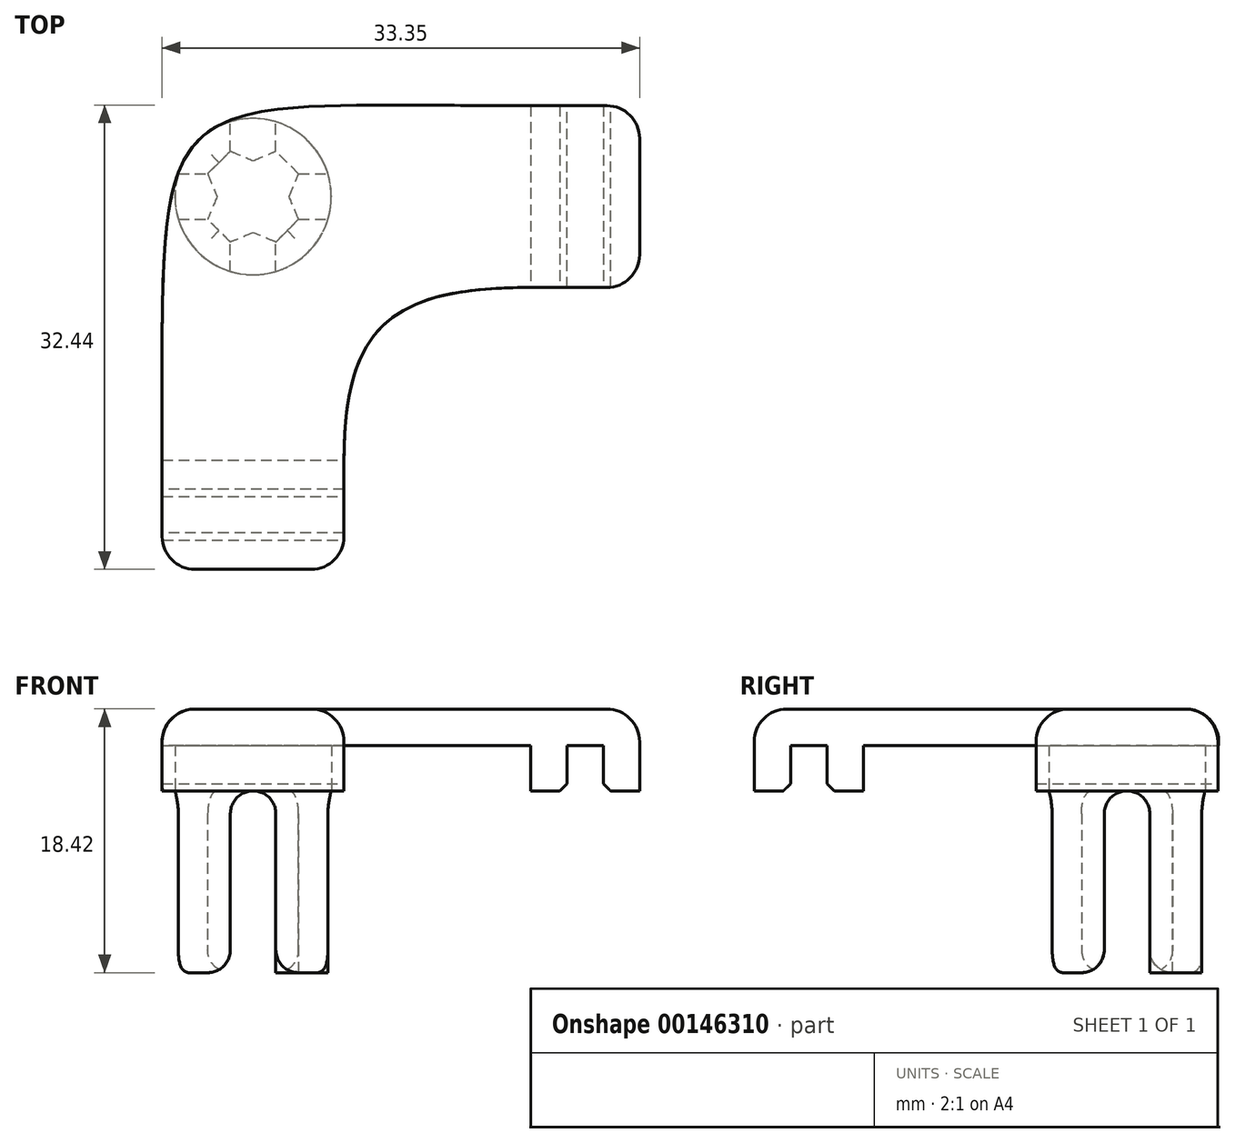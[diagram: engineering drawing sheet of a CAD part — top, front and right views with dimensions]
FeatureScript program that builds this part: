
annotation { "Feature Type Name" : "Feature", "Feature Type Description" : "" }
export const myFeature = defineFeature(function(context is Context, id is Id, definition is map)
    precondition{}
    {
        {
            var Q0;
            Q0=qCreatedBy(makeId("Top.planeOp"),FACE);
            var sketch = newSketch(context, id + "F0", { "sketchPlane" : qUnion([Q0])});
            skCircle(sketch, "E0", {"center": v(0, 0) * mm, "radius": 5.46 * mm});
            skLineSegment(sketch, "E1.bottom", {"start": v(6.35, -26.04) * mm, "end": v(-6.35, -26.04) * mm});
            skLineSegment(sketch, "E1.top", {"start": v(6.35, -18.41) * mm, "end": v(-6.35, -18.41) * mm});
            skLineSegment(sketch, "E1.left", {"start": v(6.35, -26.04) * mm, "end": v(6.35, -18.42) * mm});
            skLineSegment(sketch, "E1.right", {"start": v(-6.35, -26.04) * mm, "end": v(-6.35, -18.41) * mm});
            skPoint(sketch, "E1.middle", {"position": v(0, -22.23) * mm});
            skLineSegment(sketch, "E2.bottom", {"start": v(26.99, -6.35) * mm, "end": v(19.37, -6.35) * mm});
            skLineSegment(sketch, "E2.top", {"start": v(26.99, 6.35) * mm, "end": v(19.37, 6.35) * mm});
            skLineSegment(sketch, "E2.left", {"start": v(26.99, -6.35) * mm, "end": v(26.99, 6.35) * mm});
            skLineSegment(sketch, "E2.right", {"start": v(19.37, -6.35) * mm, "end": v(19.37, 6.35) * mm});
            skPoint(sketch, "E2.middle", {"position": v(23.18, 0) * mm});
            skSolve(sketch);
        }
        {
            var Q0;
            Q0 = qSketchRegion(id + "F0", true);
            extrude(context, id + "F1", {"entities" : qUnion([Q0]), "depth" : 15.88 * mm});
        }
        {
            var Q0;
            Q0=makeQuery(id+"F1.opExtrude","CAP_FACE",FACE,{"disambiguationData":[OSD([sQuery(id+"F0.wireOp",EDGE,"E0")])],"isStart":false});
            var sketch = newSketch(context, id + "F2", { "sketchPlane" : qUnion([Q0])});
            skLineSegment(sketch, "E3.0.0", {"start": v(-6.35, -26.04) * mm, "end": v(6.35, -26.04) * mm});
            skLineSegment(sketch, "E3.0.1", {"start": v(6.35, -26.04) * mm, "end": v(6.35, -18.42) * mm});
            skLineSegment(sketch, "E3.0.2", {"start": v(6.35, -18.41) * mm, "end": v(-6.35, -18.41) * mm});
            skLineSegment(sketch, "E3.0.3", {"start": v(-6.35, -18.41) * mm, "end": v(-6.35, -26.04) * mm});
            skLineSegment(sketch, "E4.0.0", {"start": v(19.37, -6.35) * mm, "end": v(26.99, -6.35) * mm});
            skLineSegment(sketch, "E4.0.1", {"start": v(26.99, -6.35) * mm, "end": v(26.99, 6.35) * mm});
            skLineSegment(sketch, "E4.0.2", {"start": v(26.99, 6.35) * mm, "end": v(19.37, 6.35) * mm});
            skLineSegment(sketch, "E4.0.3", {"start": v(19.37, 6.35) * mm, "end": v(19.37, -6.35) * mm});
            skCircle(sketch, "E5.0.0", {"center": v(0, 0) * mm, "radius": 5.46 * mm});
            skFitSpline(sketch, "E6", {"points": [v(-6.35, -18.41) * mm, v(19.37, 6.35) * mm], "startDerivative": vector(0, 81.2) * mm, "endDerivative": vector(81.2, 0) * mm});
            skLineSegment(sketch, "E7", {"start": v(-6.35, -18.41) * mm, "end": v(-6.35, 8.65) * mm, "construction": true});
            skLineSegment(sketch, "E8", {"start": v(-7.7, 6.35) * mm, "end": v(19.37, 6.35) * mm, "construction": true});
            skFitSpline(sketch, "E9", {"points": [v(6.35, -18.42) * mm, v(19.37, -6.35) * mm], "startDerivative": vector(0, 28.58) * mm, "endDerivative": vector(28.57, 0) * mm});
            skSolve(sketch);
        }
        {
            var Q0;
            Q0 = qSketchRegion(id + "F2", true);
            extrude(context, id + "F3", {"entities" : qUnion([Q0]), "operationType" : NewBodyOperationType.ADD, "depth" : 2.54 * mm});
        }
        {
            var Q0;
            Q0=makeQuery(id+"F1.opExtrude","CAP_EDGE",EDGE,{"disambiguationData":[OSD([sQuery(id+"F0.wireOp",EDGE,"E0")])],"isStart":false});
            var Q1;
            Q1=makeQuery(id+"F1.opExtrude","CAP_EDGE",EDGE,{"disambiguationData":[OSD([sQuery(id+"F0.wireOp",EDGE,"E1.top")])],"isStart":false});
            var Q2;
            Q2=makeQuery(id+"F1.opExtrude","CAP_EDGE",EDGE,{"disambiguationData":[OSD([sQuery(id+"F0.wireOp",EDGE,"E2.right")])],"isStart":false});
            var Q3;
            Q3=makeQuery(id+"F3.boolean.opBoolean","MERGE",EDGE,{"derivedFrom":[makeQuery(id+"F1.opExtrude","SWEPT_EDGE",EDGE,{"disambiguationData":[OSD([sQuery(id+"F0.wireOp",EDGE,"E2.bottom"),sQuery(id+"F0.wireOp",EDGE,"E2.left")])]}),makeQuery(id+"F3.opExtrude","SWEPT_EDGE",EDGE,{"disambiguationData":[OSD([sQuery(id+"F2.wireOp",EDGE,"E4.0.0"),sQuery(id+"F2.wireOp",EDGE,"E4.0.1")])]})]});
            var Q4;
            Q4=makeQuery(id+"F3.boolean.opBoolean","MERGE",EDGE,{"derivedFrom":[makeQuery(id+"F1.opExtrude","SWEPT_EDGE",EDGE,{"disambiguationData":[OSD([sQuery(id+"F0.wireOp",EDGE,"E2.top"),sQuery(id+"F0.wireOp",EDGE,"E2.left")])]}),makeQuery(id+"F3.opExtrude","SWEPT_EDGE",EDGE,{"disambiguationData":[OSD([sQuery(id+"F2.wireOp",EDGE,"E4.0.1"),sQuery(id+"F2.wireOp",EDGE,"E4.0.2")])]})]});
            var Q5;
            Q5=makeQuery(id+"F3.boolean.opBoolean","MERGE",EDGE,{"derivedFrom":[makeQuery(id+"F1.opExtrude","SWEPT_EDGE",EDGE,{"disambiguationData":[OSD([sQuery(id+"F0.wireOp",EDGE,"E1.bottom"),sQuery(id+"F0.wireOp",EDGE,"E1.left")])]}),makeQuery(id+"F3.opExtrude","SWEPT_EDGE",EDGE,{"disambiguationData":[OSD([sQuery(id+"F2.wireOp",EDGE,"E3.0.0"),sQuery(id+"F2.wireOp",EDGE,"E3.0.1")])]})]});
            var Q6;
            Q6=makeQuery(id+"F3.boolean.opBoolean","MERGE",EDGE,{"derivedFrom":[makeQuery(id+"F1.opExtrude","SWEPT_EDGE",EDGE,{"disambiguationData":[OSD([sQuery(id+"F0.wireOp",EDGE,"E1.bottom"),sQuery(id+"F0.wireOp",EDGE,"E1.right")])]}),makeQuery(id+"F3.opExtrude","SWEPT_EDGE",EDGE,{"disambiguationData":[OSD([sQuery(id+"F2.wireOp",EDGE,"E3.0.0"),sQuery(id+"F2.wireOp",EDGE,"E3.0.3")])]})]});
            var Q7;
            Q7=makeQuery(id+"F3.opExtrude","CAP_EDGE",EDGE,{"disambiguationData":[OSD([sQuery(id+"F2.wireOp",EDGE,"E6")])],"isStart":false});
            var Q8;
            Q8=makeQuery(id+"F3.opExtrude","CAP_EDGE",EDGE,{"disambiguationData":[OSD([sQuery(id+"F2.wireOp",EDGE,"E3.0.0")])],"isStart":false});
            var Q9;
            Q9=makeQuery(id+"F3.opExtrude","CAP_EDGE",EDGE,{"disambiguationData":[OSD([sQuery(id+"F2.wireOp",EDGE,"E9")])],"isStart":false});
            var Q10;
            Q10=makeQuery(id+"F3.opExtrude","CAP_EDGE",EDGE,{"disambiguationData":[OSD([sQuery(id+"F2.wireOp",EDGE,"E4.0.1")])],"isStart":false});
            fillet(context, id + "F4", {"entities" : qUnion([Q0, Q1, Q2, Q3, Q4, Q5, Q6, Q7, Q8, Q9, Q10]), "radius" : 2.3 * mm, "tangentPropagation" : true, "allowEdgeOverflow" : false});
        }
        {
            var Q0;
            Q0=makeQuery(id+"F1.opExtrude","CAP_FACE",FACE,{"disambiguationData":[OSD([sQuery(id+"F0.wireOp",EDGE,"E2.bottom"),sQuery(id+"F0.wireOp",EDGE,"E2.top"),sQuery(id+"F0.wireOp",EDGE,"E2.left"),sQuery(id+"F0.wireOp",EDGE,"E2.right")])],"isStart":true});
            var sketch = newSketch(context, id + "F5", { "sketchPlane" : qUnion([Q0])});
            skLineSegment(sketch, "E10", {"start": v(0, 18.41) * mm, "end": v(0, 26.04) * mm, "construction": true});
            skLineSegment(sketch, "E11", {"start": v(19.37, 0) * mm, "end": v(26.99, 0) * mm, "construction": true});
            skLineSegment(sketch, "E12.bottom", {"start": v(6.35, 20.96) * mm, "end": v(-6.35, 20.96) * mm});
            skLineSegment(sketch, "E12.top", {"start": v(6.35, 23.5) * mm, "end": v(-6.35, 23.5) * mm});
            skLineSegment(sketch, "E12.left", {"start": v(6.35, 20.96) * mm, "end": v(6.35, 23.5) * mm});
            skLineSegment(sketch, "E12.right", {"start": v(-6.35, 20.96) * mm, "end": v(-6.35, 23.5) * mm});
            skPoint(sketch, "E12.middle", {"position": v(0, 22.23) * mm});
            skLineSegment(sketch, "E13.bottom", {"start": v(21.9, 6.35) * mm, "end": v(24.45, 6.35) * mm});
            skLineSegment(sketch, "E13.top", {"start": v(21.9, -6.35) * mm, "end": v(24.45, -6.35) * mm});
            skLineSegment(sketch, "E13.left", {"start": v(21.9, 6.35) * mm, "end": v(21.9, -6.35) * mm});
            skLineSegment(sketch, "E13.right", {"start": v(24.45, 6.35) * mm, "end": v(24.45, -6.35) * mm});
            skPoint(sketch, "E13.middle", {"position": v(23.18, 0) * mm});
            skSolve(sketch);
        }
        {
            var Q0;
            Q0 = qSketchRegion(id + "F5", true);
            extrude(context, id + "F6", {"entities" : qUnion([Q0]), "operationType" : NewBodyOperationType.REMOVE, "oppositeDirection" : true, "depth" : 15.88 * mm});
        }
        {
            var Q0;
            Q0=makeQuery(id+"F1.opExtrude","CAP_FACE",FACE,{"disambiguationData":[OSD([sQuery(id+"F0.wireOp",EDGE,"E0")])],"isStart":true});
            var sketch = newSketch(context, id + "F7", { "sketchPlane" : qUnion([Q0])});
            skLineSegment(sketch, "E14.bottom", {"start": v(-6.35, 18.41) * mm, "end": v(6.35, 18.41) * mm});
            skLineSegment(sketch, "E14.top", {"start": v(-6.35, 26.04) * mm, "end": v(6.35, 26.04) * mm});
            skLineSegment(sketch, "E14.left", {"start": v(-6.35, 18.41) * mm, "end": v(-6.35, 26.04) * mm});
            skLineSegment(sketch, "E14.right", {"start": v(6.35, 18.41) * mm, "end": v(6.35, 26.04) * mm});
            skLineSegment(sketch, "E15.bottom", {"start": v(19.37, -6.35) * mm, "end": v(26.99, -6.35) * mm});
            skLineSegment(sketch, "E15.top", {"start": v(19.37, 6.35) * mm, "end": v(26.99, 6.35) * mm});
            skLineSegment(sketch, "E15.left", {"start": v(19.37, -6.35) * mm, "end": v(19.37, 6.35) * mm});
            skLineSegment(sketch, "E15.right", {"start": v(26.99, -6.35) * mm, "end": v(26.99, 6.35) * mm});
            skSolve(sketch);
        }
        {
            var Q0;
            Q0 = qSketchRegion(id + "F7", true);
            extrude(context, id + "F8", {"entities" : qUnion([Q0]), "operationType" : NewBodyOperationType.REMOVE, "oppositeDirection" : true, "depth" : 12.7 * mm});
        }
        {
            var Q0;
            Q0=makeQuery(id+"F8.boolean.opBoolean","INTERSECT",EDGE,{"derivedFrom":[makeQuery(id+"F6.boolean.opBoolean","COPY",FACE,{"derivedFrom":makeQuery(id+"F6.opExtrude","SWEPT_FACE",FACE,{"disambiguationData":[OSD([sQuery(id+"F5.wireOp",EDGE,"E12.top")])]})}),makeQuery(id+"F8.opExtrude","CAP_FACE",FACE,{"disambiguationData":[OSD([sQuery(id+"F7.wireOp",EDGE,"E14.bottom"),sQuery(id+"F7.wireOp",EDGE,"E14.top"),sQuery(id+"F7.wireOp",EDGE,"E14.left"),sQuery(id+"F7.wireOp",EDGE,"E14.right")])],"isStart":false})]});
            var Q1;
            Q1=makeQuery(id+"F8.boolean.opBoolean","INTERSECT",EDGE,{"derivedFrom":[makeQuery(id+"F6.boolean.opBoolean","COPY",FACE,{"derivedFrom":makeQuery(id+"F6.opExtrude","SWEPT_FACE",FACE,{"disambiguationData":[OSD([sQuery(id+"F5.wireOp",EDGE,"E12.bottom")])]})}),makeQuery(id+"F8.opExtrude","CAP_FACE",FACE,{"disambiguationData":[OSD([sQuery(id+"F7.wireOp",EDGE,"E14.bottom"),sQuery(id+"F7.wireOp",EDGE,"E14.top"),sQuery(id+"F7.wireOp",EDGE,"E14.left"),sQuery(id+"F7.wireOp",EDGE,"E14.right")])],"isStart":false})]});
            var Q2;
            Q2=makeQuery(id+"F8.boolean.opBoolean","INTERSECT",EDGE,{"derivedFrom":[makeQuery(id+"F6.boolean.opBoolean","COPY",FACE,{"derivedFrom":makeQuery(id+"F6.opExtrude","SWEPT_FACE",FACE,{"disambiguationData":[OSD([sQuery(id+"F5.wireOp",EDGE,"E13.left")])]})}),makeQuery(id+"F8.opExtrude","CAP_FACE",FACE,{"disambiguationData":[OSD([sQuery(id+"F7.wireOp",EDGE,"E15.bottom"),sQuery(id+"F7.wireOp",EDGE,"E15.top"),sQuery(id+"F7.wireOp",EDGE,"E15.left"),sQuery(id+"F7.wireOp",EDGE,"E15.right")])],"isStart":false})]});
            var Q3;
            Q3=makeQuery(id+"F8.boolean.opBoolean","INTERSECT",EDGE,{"derivedFrom":[makeQuery(id+"F6.boolean.opBoolean","COPY",FACE,{"derivedFrom":makeQuery(id+"F6.opExtrude","SWEPT_FACE",FACE,{"disambiguationData":[OSD([sQuery(id+"F5.wireOp",EDGE,"E13.right")])]})}),makeQuery(id+"F8.opExtrude","CAP_FACE",FACE,{"disambiguationData":[OSD([sQuery(id+"F7.wireOp",EDGE,"E15.bottom"),sQuery(id+"F7.wireOp",EDGE,"E15.top"),sQuery(id+"F7.wireOp",EDGE,"E15.left"),sQuery(id+"F7.wireOp",EDGE,"E15.right")])],"isStart":false})]});
            chamfer(context, id + "F9", {"entities" : qUnion([Q0, Q1, Q2, Q3]), "width" : 0.5 * mm, "tangentPropagation" : true});
        }
        {
            var Q0;
            Q0=makeQuery(id+"F1.opExtrude","CAP_FACE",FACE,{"disambiguationData":[OSD([sQuery(id+"F0.wireOp",EDGE,"E0")])],"isStart":true});
            var sketch = newSketch(context, id + "F10", { "sketchPlane" : qUnion([Q0])});
            skLineSegment(sketch, "E16.bottom", {"start": v(-5.46, 1.59) * mm, "end": v(5.46, 1.59) * mm});
            skLineSegment(sketch, "E16.top", {"start": v(-5.46, -1.59) * mm, "end": v(5.46, -1.59) * mm});
            skLineSegment(sketch, "E16.left", {"start": v(-5.46, 1.59) * mm, "end": v(-5.46, -1.59) * mm});
            skLineSegment(sketch, "E16.right", {"start": v(5.46, 1.59) * mm, "end": v(5.46, -1.59) * mm});
            skPoint(sketch, "E16.middle", {"position": v(0, 0) * mm});
            skLineSegment(sketch, "E17.bottom", {"start": v(1.59, 5.46) * mm, "end": v(-1.59, 5.46) * mm});
            skLineSegment(sketch, "E17.top", {"start": v(1.59, -5.46) * mm, "end": v(-1.59, -5.46) * mm});
            skLineSegment(sketch, "E17.left", {"start": v(1.59, 5.46) * mm, "end": v(1.59, -5.46) * mm});
            skLineSegment(sketch, "E17.right", {"start": v(-1.59, 5.46) * mm, "end": v(-1.59, -5.46) * mm});
            skSolve(sketch);
        }
        {
            var Q0;
            Q0 = qSketchRegion(id + "F10", true);
            extrude(context, id + "F11", {"entities" : qUnion([Q0]), "operationType" : NewBodyOperationType.REMOVE, "oppositeDirection" : true, "depth" : 12.7 * mm});
        }
        {
            var Q0;
            Q0=makeQuery(id+"F11.boolean.opBoolean","COPY",EDGE,{"derivedFrom":makeQuery(id+"F11.opExtrude","SWEPT_EDGE",EDGE,{"disambiguationData":[OSD([sQuery(id+"F10.wireOp",EDGE,"E16.bottom"),sQuery(id+"F10.wireOp",EDGE,"E17.right")])]})});
            var Q1;
            Q1=makeQuery(id+"F11.boolean.opBoolean","COPY",EDGE,{"derivedFrom":makeQuery(id+"F11.opExtrude","SWEPT_EDGE",EDGE,{"disambiguationData":[OSD([sQuery(id+"F10.wireOp",EDGE,"E16.bottom"),sQuery(id+"F10.wireOp",EDGE,"E17.left")])]})});
            var Q2;
            Q2=makeQuery(id+"F11.boolean.opBoolean","COPY",EDGE,{"derivedFrom":makeQuery(id+"F11.opExtrude","SWEPT_EDGE",EDGE,{"disambiguationData":[OSD([sQuery(id+"F10.wireOp",EDGE,"E16.top"),sQuery(id+"F10.wireOp",EDGE,"E17.right")])]})});
            var Q3;
            Q3=makeQuery(id+"F11.boolean.opBoolean","COPY",EDGE,{"derivedFrom":makeQuery(id+"F11.opExtrude","SWEPT_EDGE",EDGE,{"disambiguationData":[OSD([sQuery(id+"F10.wireOp",EDGE,"E16.top"),sQuery(id+"F10.wireOp",EDGE,"E17.left")])]})});
            chamfer(context, id + "F12", {"entities" : qUnion([Q0, Q1, Q2, Q3]), "width" : 1.59 * mm, "tangentPropagation" : true});
        }
        {
            var Q0;
            {var subQ0=sQuery(id+"F10.wireOp",EDGE,"E17.right");var subQ1=sQuery(id+"F10.wireOp",EDGE,"E16.bottom");Q0=makeQuery(id+"F12.opChamfer","BLEND_EDGE",EDGE,{"blendedFrom":[makeQuery(id+"F11.boolean.opBoolean","COPY",EDGE,{"derivedFrom":makeQuery(id+"F11.opExtrude","SWEPT_EDGE",EDGE,{"disambiguationData":[OSD([subQ1,subQ0])]})}),makeQuery(id+"F11.boolean.opBoolean","COPY",FACE,{"derivedFrom":makeQuery(id+"F11.opExtrude","CAP_FACE",FACE,{"disambiguationData":[OSD([subQ1,sQuery(id+"F10.wireOp",EDGE,"E16.top"),sQuery(id+"F10.wireOp",EDGE,"E16.left"),sQuery(id+"F10.wireOp",EDGE,"E16.right"),sQuery(id+"F10.wireOp",EDGE,"E17.bottom"),sQuery(id+"F10.wireOp",EDGE,"E17.top"),sQuery(id+"F10.wireOp",EDGE,"E17.left"),subQ0])],"isStart":false})})],"blendedInto":[makeQuery(id+"F11.boolean.opBoolean","COPY",FACE,{"derivedFrom":makeQuery(id+"F11.opExtrude","CAP_FACE",FACE,{"disambiguationData":[OSD([subQ1,sQuery(id+"F10.wireOp",EDGE,"E16.top"),sQuery(id+"F10.wireOp",EDGE,"E16.left"),sQuery(id+"F10.wireOp",EDGE,"E16.right"),sQuery(id+"F10.wireOp",EDGE,"E17.bottom"),sQuery(id+"F10.wireOp",EDGE,"E17.top"),sQuery(id+"F10.wireOp",EDGE,"E17.left"),subQ0])],"isStart":false})})]});}
            var Q1;
            {var subQ0=sQuery(id+"F10.wireOp",EDGE,"E17.left");var subQ1=sQuery(id+"F10.wireOp",EDGE,"E16.bottom");Q1=makeQuery(id+"F12.opChamfer","BLEND_EDGE",EDGE,{"blendedFrom":[makeQuery(id+"F11.boolean.opBoolean","COPY",EDGE,{"derivedFrom":makeQuery(id+"F11.opExtrude","SWEPT_EDGE",EDGE,{"disambiguationData":[OSD([subQ1,subQ0])]})}),makeQuery(id+"F11.boolean.opBoolean","COPY",FACE,{"derivedFrom":makeQuery(id+"F11.opExtrude","CAP_FACE",FACE,{"disambiguationData":[OSD([subQ1,sQuery(id+"F10.wireOp",EDGE,"E16.top"),sQuery(id+"F10.wireOp",EDGE,"E16.left"),sQuery(id+"F10.wireOp",EDGE,"E16.right"),sQuery(id+"F10.wireOp",EDGE,"E17.bottom"),sQuery(id+"F10.wireOp",EDGE,"E17.top"),subQ0,sQuery(id+"F10.wireOp",EDGE,"E17.right")])],"isStart":false})})],"blendedInto":[makeQuery(id+"F11.boolean.opBoolean","COPY",FACE,{"derivedFrom":makeQuery(id+"F11.opExtrude","CAP_FACE",FACE,{"disambiguationData":[OSD([subQ1,sQuery(id+"F10.wireOp",EDGE,"E16.top"),sQuery(id+"F10.wireOp",EDGE,"E16.left"),sQuery(id+"F10.wireOp",EDGE,"E16.right"),sQuery(id+"F10.wireOp",EDGE,"E17.bottom"),sQuery(id+"F10.wireOp",EDGE,"E17.top"),subQ0,sQuery(id+"F10.wireOp",EDGE,"E17.right")])],"isStart":false})})]});}
            var Q2;
            {var subQ0=sQuery(id+"F10.wireOp",EDGE,"E17.left");var subQ1=sQuery(id+"F10.wireOp",EDGE,"E16.top");Q2=makeQuery(id+"F12.opChamfer","BLEND_EDGE",EDGE,{"blendedFrom":[makeQuery(id+"F11.boolean.opBoolean","COPY",EDGE,{"derivedFrom":makeQuery(id+"F11.opExtrude","SWEPT_EDGE",EDGE,{"disambiguationData":[OSD([subQ1,subQ0])]})}),makeQuery(id+"F11.boolean.opBoolean","COPY",FACE,{"derivedFrom":makeQuery(id+"F11.opExtrude","CAP_FACE",FACE,{"disambiguationData":[OSD([sQuery(id+"F10.wireOp",EDGE,"E16.bottom"),subQ1,sQuery(id+"F10.wireOp",EDGE,"E16.left"),sQuery(id+"F10.wireOp",EDGE,"E16.right"),sQuery(id+"F10.wireOp",EDGE,"E17.bottom"),sQuery(id+"F10.wireOp",EDGE,"E17.top"),subQ0,sQuery(id+"F10.wireOp",EDGE,"E17.right")])],"isStart":false})})],"blendedInto":[makeQuery(id+"F11.boolean.opBoolean","COPY",FACE,{"derivedFrom":makeQuery(id+"F11.opExtrude","CAP_FACE",FACE,{"disambiguationData":[OSD([sQuery(id+"F10.wireOp",EDGE,"E16.bottom"),subQ1,sQuery(id+"F10.wireOp",EDGE,"E16.left"),sQuery(id+"F10.wireOp",EDGE,"E16.right"),sQuery(id+"F10.wireOp",EDGE,"E17.bottom"),sQuery(id+"F10.wireOp",EDGE,"E17.top"),subQ0,sQuery(id+"F10.wireOp",EDGE,"E17.right")])],"isStart":false})})]});}
            var Q3;
            {var subQ0=sQuery(id+"F10.wireOp",EDGE,"E17.right");var subQ1=sQuery(id+"F10.wireOp",EDGE,"E16.top");Q3=makeQuery(id+"F12.opChamfer","BLEND_EDGE",EDGE,{"blendedFrom":[makeQuery(id+"F11.boolean.opBoolean","COPY",EDGE,{"derivedFrom":makeQuery(id+"F11.opExtrude","SWEPT_EDGE",EDGE,{"disambiguationData":[OSD([subQ1,subQ0])]})}),makeQuery(id+"F11.boolean.opBoolean","COPY",FACE,{"derivedFrom":makeQuery(id+"F11.opExtrude","CAP_FACE",FACE,{"disambiguationData":[OSD([sQuery(id+"F10.wireOp",EDGE,"E16.bottom"),subQ1,sQuery(id+"F10.wireOp",EDGE,"E16.left"),sQuery(id+"F10.wireOp",EDGE,"E16.right"),sQuery(id+"F10.wireOp",EDGE,"E17.bottom"),sQuery(id+"F10.wireOp",EDGE,"E17.top"),sQuery(id+"F10.wireOp",EDGE,"E17.left"),subQ0])],"isStart":false})})],"blendedInto":[makeQuery(id+"F11.boolean.opBoolean","COPY",FACE,{"derivedFrom":makeQuery(id+"F11.opExtrude","CAP_FACE",FACE,{"disambiguationData":[OSD([sQuery(id+"F10.wireOp",EDGE,"E16.bottom"),subQ1,sQuery(id+"F10.wireOp",EDGE,"E16.left"),sQuery(id+"F10.wireOp",EDGE,"E16.right"),sQuery(id+"F10.wireOp",EDGE,"E17.bottom"),sQuery(id+"F10.wireOp",EDGE,"E17.top"),sQuery(id+"F10.wireOp",EDGE,"E17.left"),subQ0])],"isStart":false})})]});}
            var Q4;
            {var subQ0=sQuery(id+"F10.wireOp",EDGE,"E16.bottom");Q4=makeQuery(id+"F11.boolean.opBoolean","COPY",EDGE,{"derivedFrom":makeQuery(id+"F11.opExtrude","CAP_EDGE",EDGE,{"disambiguationData":[OSD([subQ0]),TDD([makeQuery(id+"F10.imprint","IMPRINT",EDGE,{"disambiguationData":[TD([[makeQuery(id+"F10.imprint","INTERSECT",VERTEX,{"derivedFrom":[subQ0,sQuery(id+"F10.wireOp",EDGE,"E16.left")]}),-1.0]])],"derivedFrom":subQ0}),makeQuery(id+"F10.imprint","IMPRINT",EDGE,{"disambiguationData":[TD([[makeQuery(id+"F10.imprint","INTERSECT",VERTEX,{"derivedFrom":[subQ0,sQuery(id+"F10.wireOp",EDGE,"E17.right")]}),1.0]])],"derivedFrom":subQ0})])],"isStart":false})});}
            var Q5;
            {var subQ0=sQuery(id+"F10.wireOp",EDGE,"E16.top");Q5=makeQuery(id+"F11.boolean.opBoolean","COPY",EDGE,{"derivedFrom":makeQuery(id+"F11.opExtrude","CAP_EDGE",EDGE,{"disambiguationData":[OSD([subQ0]),TDD([makeQuery(id+"F10.imprint","IMPRINT",EDGE,{"disambiguationData":[TD([[makeQuery(id+"F10.imprint","INTERSECT",VERTEX,{"derivedFrom":[subQ0,sQuery(id+"F10.wireOp",EDGE,"E16.left")]}),-1.0]])],"derivedFrom":subQ0}),makeQuery(id+"F10.imprint","IMPRINT",EDGE,{"disambiguationData":[TD([[makeQuery(id+"F10.imprint","INTERSECT",VERTEX,{"derivedFrom":[subQ0,sQuery(id+"F10.wireOp",EDGE,"E17.right")]}),1.0]])],"derivedFrom":subQ0})])],"isStart":false})});}
            var Q6;
            {var subQ0=sQuery(id+"F10.wireOp",EDGE,"E17.right");Q6=makeQuery(id+"F11.boolean.opBoolean","COPY",EDGE,{"derivedFrom":makeQuery(id+"F11.opExtrude","CAP_EDGE",EDGE,{"disambiguationData":[OSD([subQ0]),TDD([makeQuery(id+"F10.imprint","IMPRINT",EDGE,{"disambiguationData":[TD([[makeQuery(id+"F10.imprint","INTERSECT",VERTEX,{"derivedFrom":[sQuery(id+"F10.wireOp",EDGE,"E17.bottom"),subQ0]}),-1.0]])],"derivedFrom":subQ0}),makeQuery(id+"F10.imprint","IMPRINT",EDGE,{"disambiguationData":[TD([[makeQuery(id+"F10.imprint","INTERSECT",VERTEX,{"derivedFrom":[sQuery(id+"F10.wireOp",EDGE,"E16.bottom"),subQ0]}),1.0]])],"derivedFrom":subQ0})])],"isStart":false})});}
            var Q7;
            {var subQ0=sQuery(id+"F10.wireOp",EDGE,"E17.left");Q7=makeQuery(id+"F11.boolean.opBoolean","COPY",EDGE,{"derivedFrom":makeQuery(id+"F11.opExtrude","CAP_EDGE",EDGE,{"disambiguationData":[OSD([subQ0]),TDD([makeQuery(id+"F10.imprint","IMPRINT",EDGE,{"disambiguationData":[TD([[makeQuery(id+"F10.imprint","INTERSECT",VERTEX,{"derivedFrom":[sQuery(id+"F10.wireOp",EDGE,"E17.bottom"),subQ0]}),-1.0]])],"derivedFrom":subQ0}),makeQuery(id+"F10.imprint","IMPRINT",EDGE,{"disambiguationData":[TD([[makeQuery(id+"F10.imprint","INTERSECT",VERTEX,{"derivedFrom":[sQuery(id+"F10.wireOp",EDGE,"E16.bottom"),subQ0]}),1.0]])],"derivedFrom":subQ0})])],"isStart":false})});}
            var Q8;
            {var subQ0=sQuery(id+"F10.wireOp",EDGE,"E16.bottom");Q8=makeQuery(id+"F11.boolean.opBoolean","COPY",EDGE,{"derivedFrom":makeQuery(id+"F11.opExtrude","CAP_EDGE",EDGE,{"disambiguationData":[OSD([subQ0]),TDD([makeQuery(id+"F10.imprint","IMPRINT",EDGE,{"disambiguationData":[TD([[makeQuery(id+"F10.imprint","INTERSECT",VERTEX,{"derivedFrom":[subQ0,sQuery(id+"F10.wireOp",EDGE,"E17.left")]}),-1.0]])],"derivedFrom":subQ0}),makeQuery(id+"F10.imprint","IMPRINT",EDGE,{"disambiguationData":[TD([[makeQuery(id+"F10.imprint","INTERSECT",VERTEX,{"derivedFrom":[subQ0,sQuery(id+"F10.wireOp",EDGE,"E16.right")]}),1.0]])],"derivedFrom":subQ0})])],"isStart":false})});}
            var Q9;
            {var subQ0=sQuery(id+"F10.wireOp",EDGE,"E16.top");Q9=makeQuery(id+"F11.boolean.opBoolean","COPY",EDGE,{"derivedFrom":makeQuery(id+"F11.opExtrude","CAP_EDGE",EDGE,{"disambiguationData":[OSD([subQ0]),TDD([makeQuery(id+"F10.imprint","IMPRINT",EDGE,{"disambiguationData":[TD([[makeQuery(id+"F10.imprint","INTERSECT",VERTEX,{"derivedFrom":[subQ0,sQuery(id+"F10.wireOp",EDGE,"E17.left")]}),-1.0]])],"derivedFrom":subQ0}),makeQuery(id+"F10.imprint","IMPRINT",EDGE,{"disambiguationData":[TD([[makeQuery(id+"F10.imprint","INTERSECT",VERTEX,{"derivedFrom":[subQ0,sQuery(id+"F10.wireOp",EDGE,"E16.right")]}),1.0]])],"derivedFrom":subQ0})])],"isStart":false})});}
            var Q10;
            {var subQ0=sQuery(id+"F10.wireOp",EDGE,"E17.left");Q10=makeQuery(id+"F11.boolean.opBoolean","COPY",EDGE,{"derivedFrom":makeQuery(id+"F11.opExtrude","CAP_EDGE",EDGE,{"disambiguationData":[OSD([subQ0]),TDD([makeQuery(id+"F10.imprint","IMPRINT",EDGE,{"disambiguationData":[TD([[makeQuery(id+"F10.imprint","INTERSECT",VERTEX,{"derivedFrom":[sQuery(id+"F10.wireOp",EDGE,"E16.top"),subQ0]}),-1.0]])],"derivedFrom":subQ0}),makeQuery(id+"F10.imprint","IMPRINT",EDGE,{"disambiguationData":[TD([[makeQuery(id+"F10.imprint","INTERSECT",VERTEX,{"derivedFrom":[sQuery(id+"F10.wireOp",EDGE,"E17.top"),subQ0]}),1.0]])],"derivedFrom":subQ0})])],"isStart":false})});}
            var Q11;
            {var subQ0=sQuery(id+"F10.wireOp",EDGE,"E17.right");Q11=makeQuery(id+"F11.boolean.opBoolean","COPY",EDGE,{"derivedFrom":makeQuery(id+"F11.opExtrude","CAP_EDGE",EDGE,{"disambiguationData":[OSD([subQ0]),TDD([makeQuery(id+"F10.imprint","IMPRINT",EDGE,{"disambiguationData":[TD([[makeQuery(id+"F10.imprint","INTERSECT",VERTEX,{"derivedFrom":[sQuery(id+"F10.wireOp",EDGE,"E16.top"),subQ0]}),-1.0]])],"derivedFrom":subQ0}),makeQuery(id+"F10.imprint","IMPRINT",EDGE,{"disambiguationData":[TD([[makeQuery(id+"F10.imprint","INTERSECT",VERTEX,{"derivedFrom":[sQuery(id+"F10.wireOp",EDGE,"E17.top"),subQ0]}),1.0]])],"derivedFrom":subQ0})])],"isStart":false})});}
            fillet(context, id + "F13", {"entities" : qUnion([Q0, Q1, Q2, Q3, Q4, Q5, Q6, Q7, Q8, Q9, Q10, Q11]), "radius" : 1.59 * mm, "tangentPropagation" : true, "allowEdgeOverflow" : false});
        }
        {
            var Q0;
            {var subQ0=sQuery(id+"F10.wireOp",EDGE,"E16.top");Q0=makeQuery(id+"F11.boolean.opBoolean","COPY",EDGE,{"derivedFrom":makeQuery(id+"F11.opExtrude","CAP_EDGE",EDGE,{"disambiguationData":[OSD([subQ0]),TDD([makeQuery(id+"F10.imprint","IMPRINT",EDGE,{"disambiguationData":[TD([[makeQuery(id+"F10.imprint","INTERSECT",VERTEX,{"derivedFrom":[subQ0,sQuery(id+"F10.wireOp",EDGE,"E17.left")]}),-1.0]])],"derivedFrom":subQ0}),makeQuery(id+"F10.imprint","IMPRINT",EDGE,{"disambiguationData":[TD([[makeQuery(id+"F10.imprint","INTERSECT",VERTEX,{"derivedFrom":[subQ0,sQuery(id+"F10.wireOp",EDGE,"E16.right")]}),1.0]])],"derivedFrom":subQ0})])],"isStart":true})});}
            var Q1;
            {var subQ0=sQuery(id+"F10.wireOp",EDGE,"E17.left");Q1=makeQuery(id+"F11.boolean.opBoolean","COPY",EDGE,{"derivedFrom":makeQuery(id+"F11.opExtrude","CAP_EDGE",EDGE,{"disambiguationData":[OSD([subQ0]),TDD([makeQuery(id+"F10.imprint","IMPRINT",EDGE,{"disambiguationData":[TD([[makeQuery(id+"F10.imprint","INTERSECT",VERTEX,{"derivedFrom":[sQuery(id+"F10.wireOp",EDGE,"E16.top"),subQ0]}),-1.0]])],"derivedFrom":subQ0}),makeQuery(id+"F10.imprint","IMPRINT",EDGE,{"disambiguationData":[TD([[makeQuery(id+"F10.imprint","INTERSECT",VERTEX,{"derivedFrom":[sQuery(id+"F10.wireOp",EDGE,"E17.top"),subQ0]}),1.0]])],"derivedFrom":subQ0})])],"isStart":true})});}
            var Q2;
            {var subQ0=sQuery(id+"F10.wireOp",EDGE,"E17.right");Q2=makeQuery(id+"F11.boolean.opBoolean","COPY",EDGE,{"derivedFrom":makeQuery(id+"F11.opExtrude","CAP_EDGE",EDGE,{"disambiguationData":[OSD([subQ0]),TDD([makeQuery(id+"F10.imprint","IMPRINT",EDGE,{"disambiguationData":[TD([[makeQuery(id+"F10.imprint","INTERSECT",VERTEX,{"derivedFrom":[sQuery(id+"F10.wireOp",EDGE,"E16.top"),subQ0]}),-1.0]])],"derivedFrom":subQ0}),makeQuery(id+"F10.imprint","IMPRINT",EDGE,{"disambiguationData":[TD([[makeQuery(id+"F10.imprint","INTERSECT",VERTEX,{"derivedFrom":[sQuery(id+"F10.wireOp",EDGE,"E17.top"),subQ0]}),1.0]])],"derivedFrom":subQ0})])],"isStart":true})});}
            var Q3;
            {var subQ0=sQuery(id+"F10.wireOp",EDGE,"E16.top");Q3=makeQuery(id+"F11.boolean.opBoolean","COPY",EDGE,{"derivedFrom":makeQuery(id+"F11.opExtrude","CAP_EDGE",EDGE,{"disambiguationData":[OSD([subQ0]),TDD([makeQuery(id+"F10.imprint","IMPRINT",EDGE,{"disambiguationData":[TD([[makeQuery(id+"F10.imprint","INTERSECT",VERTEX,{"derivedFrom":[subQ0,sQuery(id+"F10.wireOp",EDGE,"E16.left")]}),-1.0]])],"derivedFrom":subQ0}),makeQuery(id+"F10.imprint","IMPRINT",EDGE,{"disambiguationData":[TD([[makeQuery(id+"F10.imprint","INTERSECT",VERTEX,{"derivedFrom":[subQ0,sQuery(id+"F10.wireOp",EDGE,"E17.right")]}),1.0]])],"derivedFrom":subQ0})])],"isStart":true})});}
            var Q4;
            {var subQ0=sQuery(id+"F10.wireOp",EDGE,"E16.bottom");Q4=makeQuery(id+"F11.boolean.opBoolean","COPY",EDGE,{"derivedFrom":makeQuery(id+"F11.opExtrude","CAP_EDGE",EDGE,{"disambiguationData":[OSD([subQ0]),TDD([makeQuery(id+"F10.imprint","IMPRINT",EDGE,{"disambiguationData":[TD([[makeQuery(id+"F10.imprint","INTERSECT",VERTEX,{"derivedFrom":[subQ0,sQuery(id+"F10.wireOp",EDGE,"E16.left")]}),-1.0]])],"derivedFrom":subQ0}),makeQuery(id+"F10.imprint","IMPRINT",EDGE,{"disambiguationData":[TD([[makeQuery(id+"F10.imprint","INTERSECT",VERTEX,{"derivedFrom":[subQ0,sQuery(id+"F10.wireOp",EDGE,"E17.right")]}),1.0]])],"derivedFrom":subQ0})])],"isStart":true})});}
            var Q5;
            {var subQ0=sQuery(id+"F10.wireOp",EDGE,"E17.right");Q5=makeQuery(id+"F11.boolean.opBoolean","COPY",EDGE,{"derivedFrom":makeQuery(id+"F11.opExtrude","CAP_EDGE",EDGE,{"disambiguationData":[OSD([subQ0]),TDD([makeQuery(id+"F10.imprint","IMPRINT",EDGE,{"disambiguationData":[TD([[makeQuery(id+"F10.imprint","INTERSECT",VERTEX,{"derivedFrom":[sQuery(id+"F10.wireOp",EDGE,"E17.bottom"),subQ0]}),-1.0]])],"derivedFrom":subQ0}),makeQuery(id+"F10.imprint","IMPRINT",EDGE,{"disambiguationData":[TD([[makeQuery(id+"F10.imprint","INTERSECT",VERTEX,{"derivedFrom":[sQuery(id+"F10.wireOp",EDGE,"E16.bottom"),subQ0]}),1.0]])],"derivedFrom":subQ0})])],"isStart":true})});}
            var Q6;
            {var subQ0=sQuery(id+"F10.wireOp",EDGE,"E17.left");Q6=makeQuery(id+"F11.boolean.opBoolean","COPY",EDGE,{"derivedFrom":makeQuery(id+"F11.opExtrude","CAP_EDGE",EDGE,{"disambiguationData":[OSD([subQ0]),TDD([makeQuery(id+"F10.imprint","IMPRINT",EDGE,{"disambiguationData":[TD([[makeQuery(id+"F10.imprint","INTERSECT",VERTEX,{"derivedFrom":[sQuery(id+"F10.wireOp",EDGE,"E17.bottom"),subQ0]}),-1.0]])],"derivedFrom":subQ0}),makeQuery(id+"F10.imprint","IMPRINT",EDGE,{"disambiguationData":[TD([[makeQuery(id+"F10.imprint","INTERSECT",VERTEX,{"derivedFrom":[sQuery(id+"F10.wireOp",EDGE,"E16.bottom"),subQ0]}),1.0]])],"derivedFrom":subQ0})])],"isStart":true})});}
            var Q7;
            {var subQ0=sQuery(id+"F10.wireOp",EDGE,"E16.bottom");Q7=makeQuery(id+"F11.boolean.opBoolean","COPY",EDGE,{"derivedFrom":makeQuery(id+"F11.opExtrude","CAP_EDGE",EDGE,{"disambiguationData":[OSD([subQ0]),TDD([makeQuery(id+"F10.imprint","IMPRINT",EDGE,{"disambiguationData":[TD([[makeQuery(id+"F10.imprint","INTERSECT",VERTEX,{"derivedFrom":[subQ0,sQuery(id+"F10.wireOp",EDGE,"E17.left")]}),-1.0]])],"derivedFrom":subQ0}),makeQuery(id+"F10.imprint","IMPRINT",EDGE,{"disambiguationData":[TD([[makeQuery(id+"F10.imprint","INTERSECT",VERTEX,{"derivedFrom":[subQ0,sQuery(id+"F10.wireOp",EDGE,"E16.right")]}),1.0]])],"derivedFrom":subQ0})])],"isStart":true})});}
            fillet(context, id + "F14", {"entities" : qUnion([Q0, Q1, Q2, Q3, Q4, Q5, Q6, Q7]), "radius" : 1.59 * mm, "tangentPropagation" : true, "allowEdgeOverflow" : false});
        }
    });
